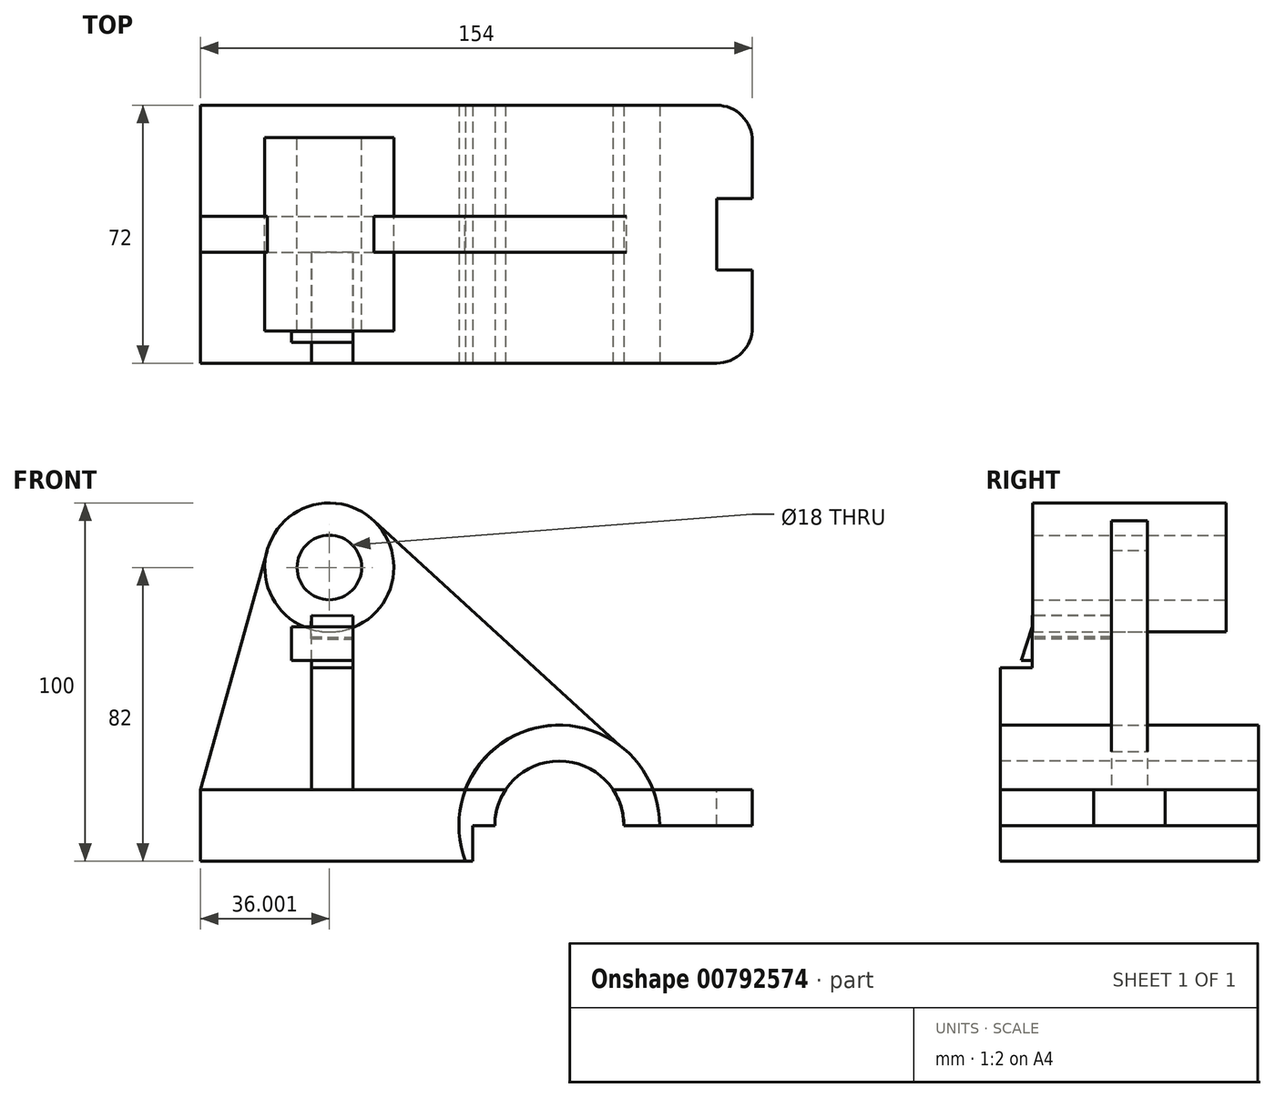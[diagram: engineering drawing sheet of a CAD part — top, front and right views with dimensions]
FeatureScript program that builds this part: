
annotation { "Feature Type Name" : "Feature", "Feature Type Description" : "" }
export const myFeature = defineFeature(function(context is Context, id is Id, definition is map)
    precondition{}
    {
        {
            var Q0;
            Q0=qCreatedBy(makeId("Front.planeOp"),FACE);
            var sketch = newSketch(context, id + "F0", { "sketchPlane" : qUnion([Q0])});
            skLineSegment(sketch, "E0.bottom", {"start": v(-34.99, 20) * mm, "end": v(119.01, 20) * mm});
            skLineSegment(sketch, "E0.top", {"start": v(-34.99, 0) * mm, "end": v(119.01, 0) * mm});
            skLineSegment(sketch, "E0.left", {"start": v(-34.99, 20) * mm, "end": v(-34.99, 0) * mm});
            skLineSegment(sketch, "E0.right", {"start": v(119.01, 20) * mm, "end": v(119.01, 0) * mm});
            skLineSegment(sketch, "E1", {"start": v(41.01, 10) * mm, "end": v(119.01, 10) * mm});
            skLineSegment(sketch, "E2", {"start": v(41.01, 10) * mm, "end": v(41.01, 0) * mm});
            skSolve(sketch);
        }
        {
            var Q0;
            Q0=makeQuery(id+"F0.imprint","IMPRINT",FACE,{"disambiguationData":[TD([[makeQuery(id+"F0.imprint","IMPRINT",EDGE,{"derivedFrom":sQuery(id+"F0.wireOp",EDGE,"E0.bottom")}),-1.0]])]});
            extrude(context, id + "F1", {"entities" : qUnion([Q0]), "endBound" : BoundingType.SYMMETRIC, "oppositeDirection" : true, "depth" : 72 * mm, "offsetDistance" : 25 * mm});
        }
        {
            var Q0;
            Q0=qCreatedBy(makeId("Front.planeOp"),FACE);
            var sketch = newSketch(context, id + "F2", { "sketchPlane" : qUnion([Q0])});
            skCircle(sketch, "E3", {"center": v(1.01, 82) * mm, "radius": 9 * mm});
            skCircle(sketch, "E4", {"center": v(1.01, 82) * mm, "radius": 18 * mm});
            skSolve(sketch);
        }
        {
            var Q0;
            Q0=makeQuery(id+"F2.imprint","IMPRINT",FACE,{"disambiguationData":[TD([[makeQuery(id+"F2.imprint","IMPRINT",EDGE,{"derivedFrom":sQuery(id+"F2.wireOp",EDGE,"E3")}),-1.0]])]});
            extrude(context, id + "F3", {"entities" : qUnion([Q0]), "endBound" : BoundingType.SYMMETRIC, "depth" : 54 * mm, "offsetDistance" : 25 * mm});
        }
        {
            var Q0;
            Q0=makeQuery(id+"F2.imprint","IMPRINT",FACE,{"disambiguationData":[TD([[makeQuery(id+"F2.imprint","IMPRINT",EDGE,{"derivedFrom":sQuery(id+"F2.wireOp",EDGE,"E3")}),-1.0]])]});
            var sketch = newSketch(context, id + "F4", { "sketchPlane" : qUnion([Q0])});
            skCircle(sketch, "E5", {"center": v(65.01, 10) * mm, "radius": 18 * mm});
            skCircle(sketch, "E6", {"center": v(65.01, 10) * mm, "radius": 28 * mm});
            skCircle(sketch, "E7.0", {"center": v(1.01, 82) * mm, "radius": 9 * mm});
            skCircle(sketch, "E7.1", {"center": v(1.01, 82) * mm, "radius": 18 * mm});
            skLineSegment(sketch, "E8", {"start": v(12.84, 95.56) * mm, "end": v(83.9, 30.68) * mm});
            skLineSegment(sketch, "E9.0", {"start": v(-34.99, 20) * mm, "end": v(119.01, 20) * mm});
            skLineSegment(sketch, "E9.1", {"start": v(-34.99, 20) * mm, "end": v(-34.99, 0) * mm});
            skLineSegment(sketch, "E10", {"start": v(-34.99, 20) * mm, "end": v(-16.33, 86.84) * mm});
            skSolve(sketch);
        }
        {
            var Q0;
            {var subQ0=sQuery(id+"F4.wireOp",EDGE,"E10");Q0=makeQuery(id+"F4.imprint","IMPRINT",FACE,{"disambiguationData":[TD([[makeQuery(id+"F4.imprint","IMPRINT",EDGE,{"derivedFrom":subQ0}),-1.0]])]});}
            extrude(context, id + "F5", {"entities" : qUnion([Q0]), "endBound" : BoundingType.SYMMETRIC, "depth" : 10 * mm, "offsetDistance" : 25 * mm});
        }
        {
            var Q0;
            Q0=makeQuery(id+"F1.opExtrude","CAP_FACE",FACE,{"disambiguationData":[OSD([sQuery(id+"F0.wireOp",EDGE,"E0.bottom"),sQuery(id+"F0.wireOp",EDGE,"E0.top"),sQuery(id+"F0.wireOp",EDGE,"E0.left"),sQuery(id+"F0.wireOp",EDGE,"E0.right"),sQuery(id+"F0.wireOp",EDGE,"E1"),sQuery(id+"F0.wireOp",EDGE,"E2")])],"isStart":true});
            var sketch = newSketch(context, id + "F6", { "sketchPlane" : qUnion([Q0])});
            skCircle(sketch, "E11", {"center": v(65.17, 10) * mm, "radius": 18 * mm});
            skCircle(sketch, "E12", {"center": v(65.17, 10) * mm, "radius": 28 * mm});
            skSolve(sketch);
        }
        {
            var Q0;
            {var subQ0=sQuery(id+"F6.wireOp",EDGE,"E11");var subQ1=makeQuery(id+"F1.opExtrude","CAP_EDGE",EDGE,{"disambiguationData":[OSD([sQuery(id+"F0.wireOp",EDGE,"E0.bottom")])],"isStart":true});var subQ2=makeQuery(id+"F6.imprint","INTERSECT",VERTEX,{"disambiguationData":[OD(0.0)],"derivedFrom":[subQ1,subQ0]});Q0=makeQuery(id+"F6.imprint","IMPRINT",FACE,{"disambiguationData":[TD([[makeQuery(id+"F6.imprint","IMPRINT",EDGE,{"disambiguationData":[TD([[subQ2,-1.0]])],"derivedFrom":subQ0}),-1.0]])]});}
            var Q1;
            {var subQ0=makeQuery(id+"F1.opExtrude","CAP_EDGE",EDGE,{"disambiguationData":[OSD([sQuery(id+"F0.wireOp",EDGE,"E2")])],"isStart":true});Q1=makeQuery(id+"F6.imprint","IMPRINT",FACE,{"disambiguationData":[TD([[makeQuery(id+"F6.imprint","IMPRINT",EDGE,{"derivedFrom":subQ0}),-1.0]])]});}
            var Q2;
            {var subQ0=sQuery(id+"F6.wireOp",EDGE,"E11");var subQ1=makeQuery(id+"F1.opExtrude","CAP_EDGE",EDGE,{"disambiguationData":[OSD([sQuery(id+"F0.wireOp",EDGE,"E0.bottom")])],"isStart":true});var subQ2=makeQuery(id+"F6.imprint","INTERSECT",VERTEX,{"disambiguationData":[OD(0.0)],"derivedFrom":[subQ1,subQ0]});Q2=makeQuery(id+"F6.imprint","IMPRINT",FACE,{"disambiguationData":[TD([[makeQuery(id+"F6.imprint","IMPRINT",EDGE,{"disambiguationData":[TD([[subQ2,1.0]])],"derivedFrom":subQ0}),-1.0]])]});}
            extrude(context, id + "F7", {"entities" : qUnion([Q0, Q1, Q2]), "oppositeDirection" : true, "depth" : 72 * mm, "offsetDistance" : 25 * mm});
        }
        {
            var Q0;
            {var subQ0=sQuery(id+"F6.wireOp",EDGE,"E11");var subQ1=makeQuery(id+"F1.opExtrude","CAP_EDGE",EDGE,{"disambiguationData":[OSD([sQuery(id+"F0.wireOp",EDGE,"E0.bottom")])],"isStart":true});var subQ2=makeQuery(id+"F6.imprint","INTERSECT",VERTEX,{"disambiguationData":[OD(0.0)],"derivedFrom":[subQ1,subQ0]});Q0=makeQuery(id+"F6.imprint","IMPRINT",FACE,{"disambiguationData":[TD([[makeQuery(id+"F6.imprint","IMPRINT",EDGE,{"disambiguationData":[TD([[subQ2,1.0]])],"derivedFrom":subQ0}),1.0]])]});}
            extrude(context, id + "F8", {"entities" : qUnion([Q0]), "operationType" : NewBodyOperationType.REMOVE, "endBound" : BoundingType.THROUGH_ALL, "oppositeDirection" : true, "depth" : 25 * mm, "offsetDistance" : 25 * mm});
        }
        {
            var Q0;
            Q0=makeQuery(id+"F1.opExtrude","CAP_EDGE",EDGE,{"disambiguationData":[OSD([sQuery(id+"F0.wireOp",EDGE,"E0.right")])],"isStart":false});
            var Q1;
            Q1=makeQuery(id+"F1.opExtrude","CAP_EDGE",EDGE,{"disambiguationData":[OSD([sQuery(id+"F0.wireOp",EDGE,"E0.right")])],"isStart":true});
            fillet(context, id + "F9", {"entities" : qUnion([Q0, Q1]), "radius" : 10 * mm, "tangentPropagation" : true, "allowEdgeOverflow" : false});
        }
        {
            var Q0;
            {var subQ2=sQuery(id+"F0.wireOp",EDGE,"E0.right");var subQ5=sQuery(id+"F0.wireOp",EDGE,"E0.bottom");Q0=makeQuery(id+"F8.boolean.opBoolean","SPLIT",FACE,{"disambiguationData":[TD([makeQuery(id+"F1.opExtrude","SWEPT_FACE",FACE,{"disambiguationData":[OSD([subQ2])]})])],"derivedFrom":makeQuery(id+"F1.opExtrude","SWEPT_FACE",FACE,{"disambiguationData":[OSD([subQ5])]})});}
            var sketch = newSketch(context, id + "F10", { "sketchPlane" : qUnion([Q0])});
            skLineSegment(sketch, "E13.bottom", {"start": v(119.01, 10) * mm, "end": v(109.01, 10) * mm});
            skLineSegment(sketch, "E13.top", {"start": v(119.01, -10) * mm, "end": v(109.01, -10) * mm});
            skLineSegment(sketch, "E13.left", {"start": v(119.01, 10) * mm, "end": v(119.01, -10) * mm});
            skLineSegment(sketch, "E13.right", {"start": v(109.01, 10) * mm, "end": v(109.01, -10) * mm});
            skSolve(sketch);
        }
        {
            var Q0;
            Q0=makeQuery(id+"F10.imprint","IMPRINT",FACE,{"disambiguationData":[TD([[makeQuery(id+"F10.imprint","IMPRINT",EDGE,{"derivedFrom":sQuery(id+"F10.wireOp",EDGE,"E13.bottom")}),1.0]])]});
            extrude(context, id + "F11", {"entities" : qUnion([Q0]), "operationType" : NewBodyOperationType.REMOVE, "oppositeDirection" : true, "depth" : 25 * mm, "offsetDistance" : 25 * mm});
        }
        {
            var Q0;
            {var subQ0=sQuery(id+"F0.wireOp",EDGE,"E1");var subQ1=sQuery(id+"F0.wireOp",EDGE,"E0.left");var subQ2=sQuery(id+"F0.wireOp",EDGE,"E0.top");var subQ3=sQuery(id+"F0.wireOp",EDGE,"E0.bottom");var subQ4=sQuery(id+"F0.wireOp",EDGE,"E2");Q0=makeQuery(id+"F8.boolean.opBoolean","SPLIT",FACE,{"disambiguationData":[TD([makeQuery(id+"F1.opExtrude","SWEPT_FACE",FACE,{"disambiguationData":[OSD([subQ2])]})])],"derivedFrom":makeQuery(id+"F1.opExtrude","CAP_FACE",FACE,{"disambiguationData":[OSD([subQ3,subQ2,subQ1,sQuery(id+"F0.wireOp",EDGE,"E0.right"),subQ0,subQ4])],"isStart":true})});}
            var sketch = newSketch(context, id + "F12", { "sketchPlane" : qUnion([Q0])});
            skLineSegment(sketch, "E14", {"start": v(1.01, 20) * mm, "end": v(1.01, 69.29) * mm, "construction": true});
            skLineSegment(sketch, "E15", {"start": v(-3.99, 20) * mm, "end": v(-3.99, 68.64) * mm});
            skLineSegment(sketch, "E16", {"start": v(7.6, 20) * mm, "end": v(7.6, 68.49) * mm});
            skLineSegment(sketch, "E17", {"start": v(-3.99, 20) * mm, "end": v(7.6, 20) * mm});
            skLineSegment(sketch, "E18", {"start": v(-3.99, 68.64) * mm, "end": v(7.6, 68.49) * mm});
            skSolve(sketch);
        }
        {
            var Q0;
            Q0=makeQuery(id+"F12.imprint","IMPRINT",FACE,{"disambiguationData":[TD([[makeQuery(id+"F12.imprint","IMPRINT",EDGE,{"derivedFrom":sQuery(id+"F12.wireOp",EDGE,"E15")}),-1.0]])]});
            var Q1;
            Q1=makeQuery(id+"F5.opExtrude","CAP_FACE",FACE,{"disambiguationData":[OSD([sQuery(id+"F4.wireOp",EDGE,"E6"),sQuery(id+"F4.wireOp",EDGE,"E7.1"),sQuery(id+"F4.wireOp",EDGE,"E8"),sQuery(id+"F4.wireOp",EDGE,"E9.0"),sQuery(id+"F4.wireOp",EDGE,"E10")])],"isStart":false});
            extrude(context, id + "F13", {"entities" : qUnion([Q0]), "endBound" : BoundingType.UP_TO_SURFACE, "oppositeDirection" : true, "depth" : 31.3 * mm, "endBoundEntityFace" : qUnion([Q1]), "offsetDistance" : 25 * mm});
        }
        {
            var Q0;
            Q0=makeQuery(id+"F13.opExtrude","CAP_FACE",FACE,{"disambiguationData":[OSD([sQuery(id+"F12.wireOp",EDGE,"E15"),sQuery(id+"F12.wireOp",EDGE,"E16"),sQuery(id+"F12.wireOp",EDGE,"E17"),sQuery(id+"F12.wireOp",EDGE,"E18")])],"isStart":true});
            var sketch = newSketch(context, id + "F14", { "sketchPlane" : qUnion([Q0])});
            skLineSegment(sketch, "E19", {"start": v(-3.99, 54) * mm, "end": v(7.6, 54) * mm});
            skSolve(sketch);
        }
        {
            var Q0;
            {var subQ0=sQuery(id+"F14.wireOp",EDGE,"E19");Q0=makeQuery(id+"F14.imprint","IMPRINT",FACE,{"disambiguationData":[TD([[makeQuery(id+"F14.imprint","IMPRINT",EDGE,{"derivedFrom":subQ0}),1.0]])]});}
            extrude(context, id + "F15", {"entities" : qUnion([Q0]), "operationType" : NewBodyOperationType.REMOVE, "oppositeDirection" : true, "depth" : 8.9 * mm, "offsetDistance" : 25 * mm});
        }
        {
            var Q0;
            Q0=makeQuery(id+"F13.opExtrude","SWEPT_FACE",FACE,{"disambiguationData":[OSD([sQuery(id+"F12.wireOp",EDGE,"E16")])]});
            var sketch = newSketch(context, id + "F16", { "sketchPlane" : qUnion([Q0])});
            skLineSegment(sketch, "E20", {"start": v(-53.45, 56) * mm, "end": v(-13.65, 56) * mm});
            skLineSegment(sketch, "E21", {"start": v(-23.18, 102) * mm, "end": v(-56.55, 102) * mm});
            skLineSegment(sketch, "E22", {"start": v(-27, 65.72) * mm, "end": v(-36, 37.77) * mm});
            skLineSegment(sketch, "E23", {"start": v(-27, 65.72) * mm, "end": v(-27, 68.64) * mm});
            skSolve(sketch);
        }
        {
            var Q0;
            Q0=makeQuery(id+"F13.opExtrude","SWEPT_FACE",FACE,{"disambiguationData":[OSD([sQuery(id+"F12.wireOp",EDGE,"E18")])]});
            extrude(context, id + "F17", {"entities" : qUnion([Q0]), "oppositeDirection" : true, "depth" : 6 * mm, "offsetDistance" : 25 * mm});
        }
        {
            var Q0;
            {var subQ0=sQuery(id+"F16.wireOp",EDGE,"E22");var subQ1=sQuery(id+"F16.wireOp",EDGE,"E20");var subQ2=makeQuery(id+"F16.imprint","INTERSECT",VERTEX,{"derivedFrom":[subQ1,subQ0]});Q0=makeQuery(id+"F16.imprint","IMPRINT",FACE,{"disambiguationData":[TD([[makeQuery(id+"F16.imprint","IMPRINT",EDGE,{"disambiguationData":[TD([[subQ2,1.0]])],"derivedFrom":subQ1}),-1.0]])]});}
            extrude(context, id + "F18", {"entities" : qUnion([Q0]), "operationType" : NewBodyOperationType.REMOVE, "oppositeDirection" : true, "depth" : 34 * mm, "offsetDistance" : 25 * mm});
        }
        {
            var Q0;
            Q0=makeQuery(id+"F13.opExtrude","SWEPT_FACE",FACE,{"disambiguationData":[OSD([sQuery(id+"F12.wireOp",EDGE,"E18")])]});
            extrude(context, id + "F19", {"entities" : qUnion([Q0]), "oppositeDirection" : true, "depth" : 6.5 * mm, "offsetDistance" : 25 * mm});
        }
        {
            var Q0;
            {var subQ6=sQuery(id+"F16.wireOp",EDGE,"E22");var subQ8=sQuery(id+"F16.wireOp",EDGE,"E20");var subQ9=makeQuery(id+"F16.imprint","INTERSECT",VERTEX,{"derivedFrom":[subQ8,subQ6]});Q0=makeQuery(id+"F16.imprint","IMPRINT",FACE,{"disambiguationData":[TD([[makeQuery(id+"F16.imprint","IMPRINT",EDGE,{"disambiguationData":[TD([[subQ9,1.0]])],"derivedFrom":subQ8}),1.0]])]});}
            extrude(context, id + "F20", {"entities" : qUnion([Q0]), "oppositeDirection" : true, "depth" : 17.2 * mm, "offsetDistance" : 25 * mm});
        }
    });
